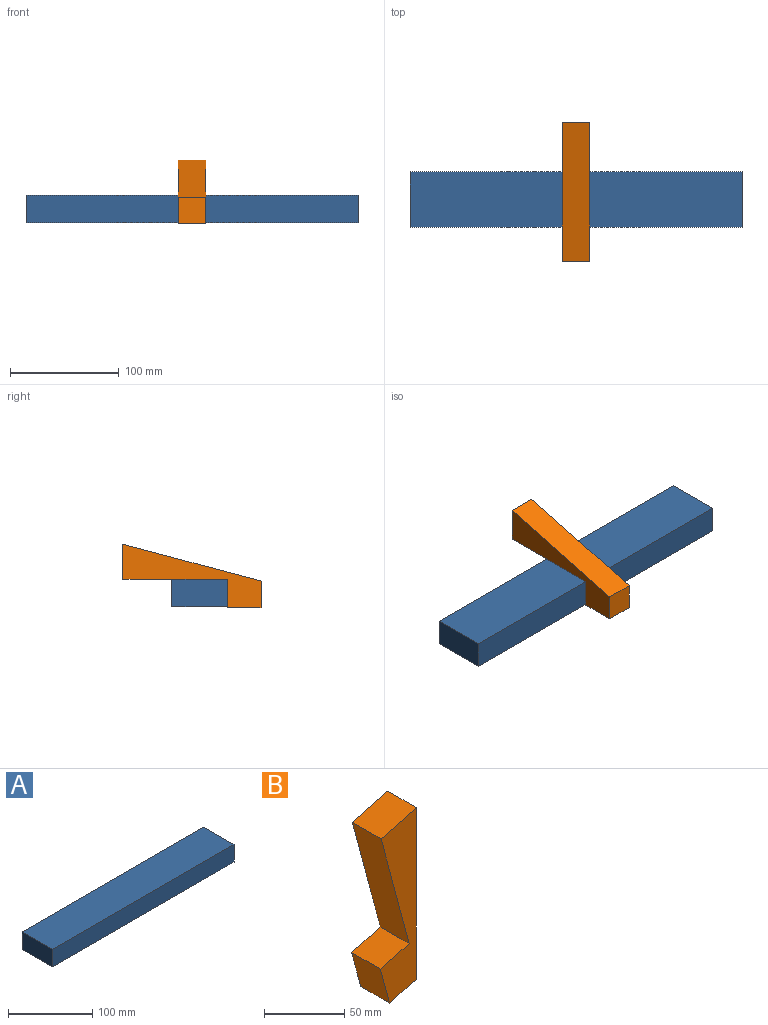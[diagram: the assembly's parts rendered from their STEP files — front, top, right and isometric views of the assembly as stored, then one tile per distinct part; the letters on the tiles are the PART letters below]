
ASSEMBLY  parts=2 mates=1
PART A: 6 faces, bbox 304.8x50.8x25.4 mm
  f0: plane 304.8x25.4mm, normal (0,-1,0), area 7741.9mm2, adj f1,f3,f4,f5
  f1: plane 50.8x25.4mm, normal (1,0,0), area 1290.3mm2, adj f0,f2,f4,f5
  f2: plane 304.8x25.4mm, normal (0,1,0), area 7741.9mm2, adj f1,f3,f4,f5
  f3: plane 50.8x25.4mm, normal (-1,0,0), area 1290.3mm2, adj f0,f2,f4,f5
  f4: plane 304.8x50.8mm, normal (0,0,1), area 15483.8mm2, adj f0,f1,f2,f3
  f5: plane 304.8x50.8mm, normal (0,0,-1), area 15483.8mm2, adj f0,f1,f2,f3
PART B: 8 faces, bbox 31.8x25.4x137.6 mm
  f0: plane 25.4x23.73mm, normal (0.26,0,-0.97), area 623.9mm2, adj f1,f5,f6,f7
  f1: plane 131.19x25.4mm, normal (1,0,0), area 3332.3mm2, adj f0,f2,f6,f7
  f2: plane 31.13x25.4mm, normal (-0.26,0,0.97), area 818.5mm2, adj f1,f3,f6,f7
  f3: plane 92.46x25.4mm, normal (-0.97,0,-0.26), area 2431.4mm2, adj f2,f4,f6,f7
  f4: plane 25.4x25.4mm, normal (-0.26,0,0.97), area 667.9mm2, adj f3,f5,f6,f7
  f5: plane 29.94x25.4mm, normal (-0.97,0,-0.26), area 787.4mm2, adj f0,f4,f6,f7
  f6: plane 137.55x31.75mm, normal (0,-1,0), area 2747.1mm2, adj f0,f1,f2,f3,f4,f5
  f7: plane 137.55x31.75mm, normal (0,1,0), area 2747.1mm2, adj f0,f1,f2,f3,f4,f5
PLACE A rot(axis=(0,0,1),180deg) t=(34.57,28.14,100.47)mm
PLACE B rot(axis=(-0.52,-0.52,-0.68),111.8deg) t=(47.27,-28.26,91.27)mm
MATE fastened B.f4 <-> A.f2  axis (0,1,0) through (34.57,2.74,125.87)mm
